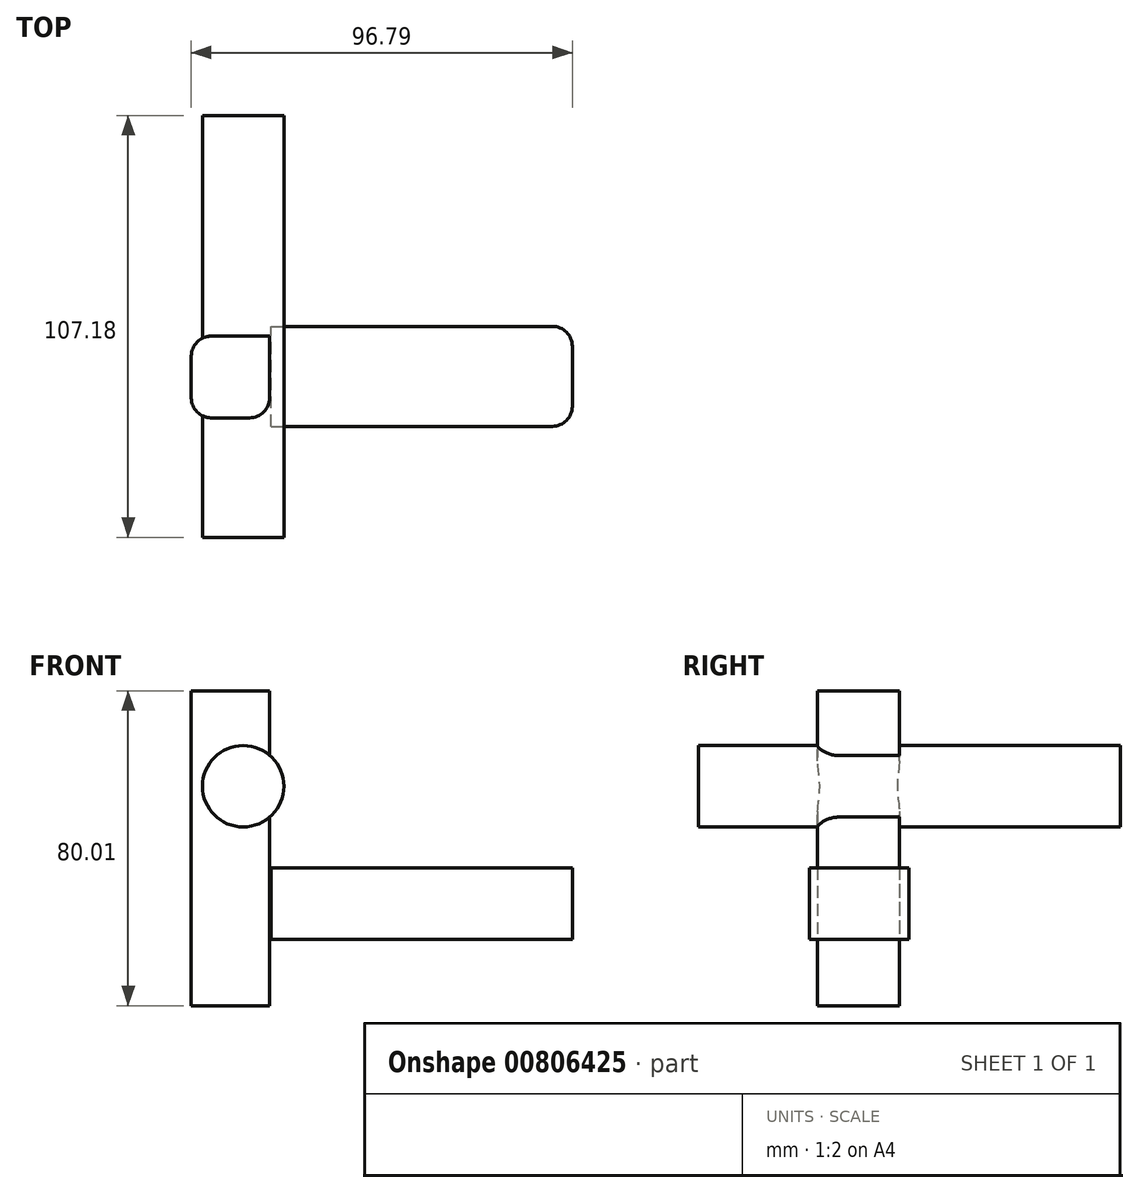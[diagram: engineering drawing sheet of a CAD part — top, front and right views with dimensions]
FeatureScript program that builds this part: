
annotation { "Feature Type Name" : "Feature", "Feature Type Description" : "" }
export const myFeature = defineFeature(function(context is Context, id is Id, definition is map)
    precondition{}
    {
        {
            var Q0;
            Q0=qCreatedBy(makeId("Front.planeOp"),FACE);
            var sketch = newSketch(context, id + "F0", { "sketchPlane" : qUnion([Q0])});
            skLineSegment(sketch, "E0.bottom", {"start": v(-33.2, 35) * mm, "end": v(43.3, 35) * mm});
            skLineSegment(sketch, "E0.top", {"start": v(-33.2, 16.86) * mm, "end": v(43.3, 16.86) * mm});
            skLineSegment(sketch, "E0.left", {"start": v(-33.2, 35) * mm, "end": v(-33.2, 16.86) * mm});
            skLineSegment(sketch, "E0.right", {"start": v(43.3, 35) * mm, "end": v(43.3, 16.86) * mm});
            skSolve(sketch);
        }
        {
            var Q0;
            Q0 = qSketchRegion(id + "F0", true);
            extrude(context, id + "F1", {"entities" : qUnion([Q0]), "depth" : 25.4 * mm, "offsetDistance" : 25.4 * mm});
        }
        {
            var Q0;
            Q0=qCreatedBy(makeId("Top.planeOp"),FACE);
            var sketch = newSketch(context, id + "F2", { "sketchPlane" : qUnion([Q0])});
            skLineSegment(sketch, "E1.bottom", {"start": v(-53.48, -23.25) * mm, "end": v(-33.58, -23.25) * mm});
            skLineSegment(sketch, "E1.top", {"start": v(-53.48, -2.5) * mm, "end": v(-33.58, -2.5) * mm});
            skLineSegment(sketch, "E1.left", {"start": v(-53.48, -23.25) * mm, "end": v(-53.48, -2.5) * mm});
            skLineSegment(sketch, "E1.right", {"start": v(-33.58, -23.25) * mm, "end": v(-33.58, -2.5) * mm});
            skSolve(sketch);
        }
        {
            var Q0;
            Q0 = qSketchRegion(id + "F2", true);
            extrude(context, id + "F3", {"entities" : qUnion([Q0]), "depth" : 80 * mm, "offsetDistance" : 25.4 * mm});
        }
        {
            var Q0;
            Q0=makeQuery(id+"F1.opExtrude","CAP_EDGE",EDGE,{"disambiguationData":[OSD([sQuery(id+"F0.wireOp",EDGE,"E0.right")])],"isStart":false});
            var Q1;
            Q1=makeQuery(id+"F1.opExtrude","CAP_EDGE",EDGE,{"disambiguationData":[OSD([sQuery(id+"F0.wireOp",EDGE,"E0.right")])],"isStart":true});
            var Q2;
            Q2=makeQuery(id+"F3.opExtrude","SWEPT_EDGE",EDGE,{"disambiguationData":[OSD([sQuery(id+"F2.wireOp",EDGE,"E1.bottom"),sQuery(id+"F2.wireOp",EDGE,"E1.right")])]});
            var Q3;
            Q3=makeQuery(id+"F3.opExtrude","SWEPT_EDGE",EDGE,{"disambiguationData":[OSD([sQuery(id+"F2.wireOp",EDGE,"E1.top"),sQuery(id+"F2.wireOp",EDGE,"E1.left")])]});
            var Q4;
            Q4=makeQuery(id+"F3.opExtrude","SWEPT_EDGE",EDGE,{"disambiguationData":[OSD([sQuery(id+"F2.wireOp",EDGE,"E1.bottom"),sQuery(id+"F2.wireOp",EDGE,"E1.left")])]});
            fillet(context, id + "F4", {"entities" : qUnion([Q0, Q1, Q2, Q3, Q4]), "radius" : 5.08 * mm, "tangentPropagation" : true, "allowEdgeOverflow" : false});
        }
        {
            var Q0;
            Q0=qCreatedBy(makeId("Front.planeOp"),FACE);
            var sketch = newSketch(context, id + "F5", { "sketchPlane" : qUnion([Q0])});
            skCircle(sketch, "E2", {"center": v(-40.3, 55.74) * mm, "radius": 10.33 * mm});
            skSolve(sketch);
        }
        {
            var Q0;
            Q0=makeQuery(id+"F5.imprint","IMPRINT",FACE,{"disambiguationData":[TD([[makeQuery(id+"F5.imprint","IMPRINT",EDGE,{"derivedFrom":sQuery(id+"F5.wireOp",EDGE,"E2")}),1.0]])]});
            extrude(context, id + "F6", {"entities" : qUnion([Q0]), "operationType" : NewBodyOperationType.ADD, "endBound" : BoundingType.SYMMETRIC, "depth" : 107.19 * mm, "offsetDistance" : 25.4 * mm});
        }
    });
